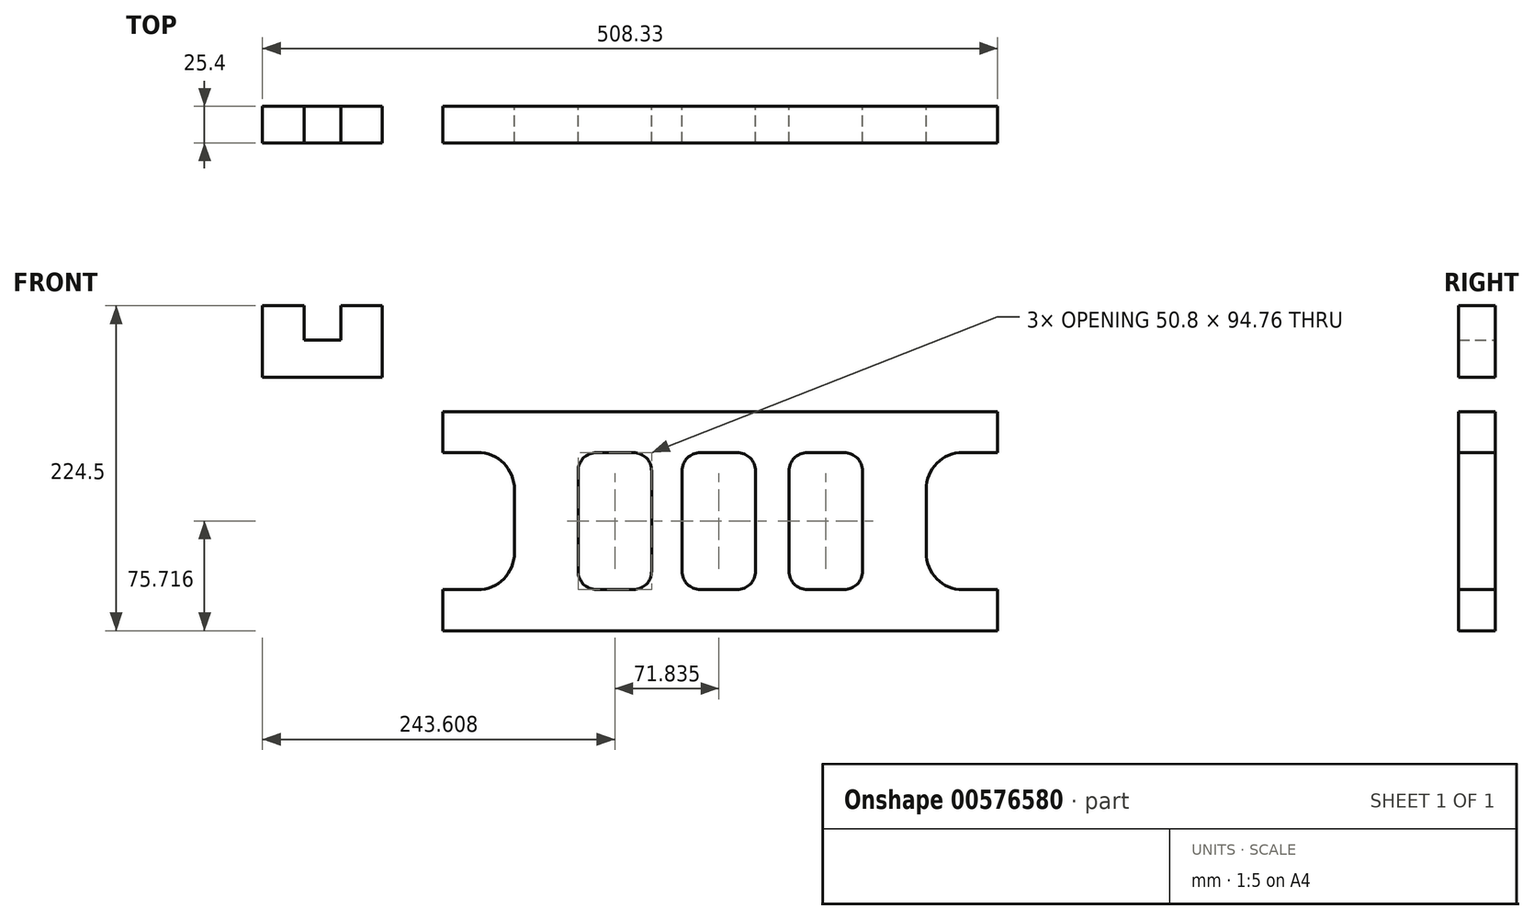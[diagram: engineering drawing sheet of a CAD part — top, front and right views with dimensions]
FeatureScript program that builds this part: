
annotation { "Feature Type Name" : "Feature", "Feature Type Description" : "" }
export const myFeature = defineFeature(function(context is Context, id is Id, definition is map)
    precondition{}
    {
        {
            var Q0;
            Q0=qCreatedBy(makeId("Front.planeOp"),FACE);
            var sketch = newSketch(context, id + "F0", { "sketchPlane" : qUnion([Q0])});
            skLineSegment(sketch, "E0", {"start": v(-25.47, 23.75) * mm, "end": v(-54.17, 23.75) * mm});
            skLineSegment(sketch, "E1", {"start": v(-54.17, 23.75) * mm, "end": v(-54.17, -25.66) * mm});
            skLineSegment(sketch, "E2", {"start": v(-54.17, -25.66) * mm, "end": v(28.7, -25.66) * mm});
            skLineSegment(sketch, "E3", {"start": v(28.7, -25.66) * mm, "end": v(28.7, 23.75) * mm});
            skLineSegment(sketch, "E4", {"start": v(28.7, 23.75) * mm, "end": v(0, 23.75) * mm});
            skLineSegment(sketch, "E5", {"start": v(0, 23.75) * mm, "end": v(0, 0) * mm});
            skLineSegment(sketch, "E6", {"start": v(0, 0) * mm, "end": v(-25.47, 0) * mm});
            skLineSegment(sketch, "E7", {"start": v(-25.47, 0) * mm, "end": v(-25.47, 23.75) * mm});
            skLineSegment(sketch, "E8", {"start": v(70.5, -49.32) * mm, "end": v(454.16, -49.32) * mm});
            skLineSegment(sketch, "E9", {"start": v(454.16, -49.32) * mm, "end": v(454.16, -77.66) * mm});
            skLineSegment(sketch, "E10", {"start": v(454.16, -77.66) * mm, "end": v(430.07, -77.66) * mm});
            skLineSegment(sketch, "E11", {"start": v(404.67, -103.06) * mm, "end": v(404.67, -147.01) * mm});
            skLineSegment(sketch, "E12", {"start": v(430.07, -172.41) * mm, "end": v(454.16, -172.41) * mm});
            skLineSegment(sketch, "E13", {"start": v(454.16, -172.41) * mm, "end": v(454.16, -200.75) * mm});
            skLineSegment(sketch, "E14", {"start": v(454.16, -200.75) * mm, "end": v(70.5, -200.75) * mm});
            skLineSegment(sketch, "E15", {"start": v(70.5, -200.75) * mm, "end": v(70.5, -172.41) * mm});
            skLineSegment(sketch, "E16", {"start": v(70.5, -172.41) * mm, "end": v(94.59, -172.41) * mm});
            skLineSegment(sketch, "E17", {"start": v(119.99, -147.01) * mm, "end": v(119.99, -103.06) * mm});
            skLineSegment(sketch, "E18", {"start": v(94.59, -77.66) * mm, "end": v(70.5, -77.66) * mm});
            skLineSegment(sketch, "E19", {"start": v(70.5, -77.66) * mm, "end": v(70.5, -49.32) * mm});
            skLineSegment(sketch, "E20", {"start": v(70.5, -49.32) * mm, "end": v(70.5, -49.32) * mm});
            skPoint(sketch, "E21.visualSharp", {"position": v(119.99, -77.66) * mm});
            skArc(sketch, "E21.filletArc", {"start": v(119.99, -103.06) * mm, "mid": v(112.55, -85.1) * mm, "end": v(94.59, -77.66) * mm});
            skPoint(sketch, "E22.visualSharp", {"position": v(119.99, -172.41) * mm});
            skArc(sketch, "E22.filletArc", {"start": v(94.59, -172.41) * mm, "mid": v(112.55, -164.97) * mm, "end": v(119.99, -147.01) * mm});
            skPoint(sketch, "E23.visualSharp", {"position": v(404.67, -77.66) * mm});
            skArc(sketch, "E23.filletArc", {"start": v(430.07, -77.66) * mm, "mid": v(412.1, -85.1) * mm, "end": v(404.67, -103.06) * mm});
            skPoint(sketch, "E24.visualSharp", {"position": v(404.67, -172.41) * mm});
            skArc(sketch, "E24.filletArc", {"start": v(404.67, -147.01) * mm, "mid": v(412.1, -164.97) * mm, "end": v(430.07, -172.41) * mm});
            skLineSegment(sketch, "E25.bottom", {"start": v(176.74, -77.66) * mm, "end": v(202.14, -77.66) * mm});
            skLineSegment(sketch, "E25.top", {"start": v(176.74, -172.41) * mm, "end": v(202.14, -172.41) * mm});
            skLineSegment(sketch, "E25.left", {"start": v(164.04, -90.36) * mm, "end": v(164.04, -159.71) * mm});
            skLineSegment(sketch, "E25.right", {"start": v(214.84, -90.36) * mm, "end": v(214.84, -159.71) * mm});
            skLineSegment(sketch, "E26.bottom", {"start": v(248.57, -77.66) * mm, "end": v(273.97, -77.66) * mm});
            skLineSegment(sketch, "E26.top", {"start": v(248.57, -172.41) * mm, "end": v(273.97, -172.41) * mm});
            skLineSegment(sketch, "E26.left", {"start": v(235.87, -90.36) * mm, "end": v(235.87, -159.71) * mm});
            skLineSegment(sketch, "E26.right", {"start": v(286.67, -90.36) * mm, "end": v(286.67, -159.71) * mm});
            skLineSegment(sketch, "E27.bottom", {"start": v(322.52, -77.66) * mm, "end": v(347.92, -77.66) * mm});
            skLineSegment(sketch, "E27.top", {"start": v(322.52, -172.41) * mm, "end": v(347.92, -172.41) * mm});
            skLineSegment(sketch, "E27.left", {"start": v(309.82, -90.36) * mm, "end": v(309.82, -159.71) * mm});
            skLineSegment(sketch, "E27.right", {"start": v(360.62, -90.36) * mm, "end": v(360.62, -159.71) * mm});
            skPoint(sketch, "E28.visualSharp", {"position": v(164.04, -77.66) * mm});
            skArc(sketch, "E28.filletArc", {"start": v(176.74, -77.66) * mm, "mid": v(167.76, -81.37) * mm, "end": v(164.04, -90.36) * mm});
            skPoint(sketch, "E29.visualSharp", {"position": v(214.84, -77.66) * mm});
            skArc(sketch, "E29.filletArc", {"start": v(214.84, -90.36) * mm, "mid": v(211.12, -81.37) * mm, "end": v(202.14, -77.66) * mm});
            skLineSegment(sketch, "E30", {"start": v(119.99, -77.66) * mm, "end": v(164.04, -77.66) * mm});
            skPoint(sketch, "E31.visualSharp", {"position": v(214.84, -172.41) * mm});
            skArc(sketch, "E31.filletArc", {"start": v(202.14, -172.41) * mm, "mid": v(211.12, -168.7) * mm, "end": v(214.84, -159.71) * mm});
            skPoint(sketch, "E32.visualSharp", {"position": v(164.04, -172.41) * mm});
            skArc(sketch, "E32.filletArc", {"start": v(164.04, -159.71) * mm, "mid": v(167.76, -168.7) * mm, "end": v(176.74, -172.41) * mm});
            skPoint(sketch, "E33.visualSharp", {"position": v(235.87, -172.41) * mm});
            skArc(sketch, "E33.filletArc", {"start": v(235.87, -159.71) * mm, "mid": v(239.6, -168.7) * mm, "end": v(248.57, -172.41) * mm});
            skPoint(sketch, "E34.visualSharp", {"position": v(235.87, -77.66) * mm});
            skArc(sketch, "E34.filletArc", {"start": v(248.57, -77.66) * mm, "mid": v(239.6, -81.37) * mm, "end": v(235.87, -90.36) * mm});
            skPoint(sketch, "E35.visualSharp", {"position": v(286.67, -77.66) * mm});
            skArc(sketch, "E35.filletArc", {"start": v(286.67, -90.36) * mm, "mid": v(282.95, -81.37) * mm, "end": v(273.97, -77.66) * mm});
            skPoint(sketch, "E36.visualSharp", {"position": v(286.67, -172.41) * mm});
            skArc(sketch, "E36.filletArc", {"start": v(273.97, -172.41) * mm, "mid": v(282.95, -168.7) * mm, "end": v(286.67, -159.71) * mm});
            skPoint(sketch, "E37.visualSharp", {"position": v(309.82, -172.41) * mm});
            skArc(sketch, "E37.filletArc", {"start": v(309.82, -159.71) * mm, "mid": v(313.54, -168.7) * mm, "end": v(322.52, -172.41) * mm});
            skPoint(sketch, "E38.visualSharp", {"position": v(360.62, -172.41) * mm});
            skArc(sketch, "E38.filletArc", {"start": v(347.92, -172.41) * mm, "mid": v(356.9, -168.7) * mm, "end": v(360.62, -159.71) * mm});
            skPoint(sketch, "E39.visualSharp", {"position": v(309.82, -77.66) * mm});
            skArc(sketch, "E39.filletArc", {"start": v(322.52, -77.66) * mm, "mid": v(313.54, -81.37) * mm, "end": v(309.82, -90.36) * mm});
            skPoint(sketch, "E40.visualSharp", {"position": v(360.62, -77.66) * mm});
            skArc(sketch, "E40.filletArc", {"start": v(360.62, -90.36) * mm, "mid": v(356.9, -81.37) * mm, "end": v(347.92, -77.66) * mm});
            skLineSegment(sketch, "E41", {"start": v(360.62, -77.66) * mm, "end": v(404.67, -77.66) * mm});
            skSolve(sketch);
        }
        {
            var Q0;
            Q0 = qSketchRegion(id + "F0", true);
            extrude(context, id + "F1", {"entities" : qUnion([Q0]), "depth" : 25.4 * mm, "offsetDistance" : 25.4 * mm});
        }
    });
